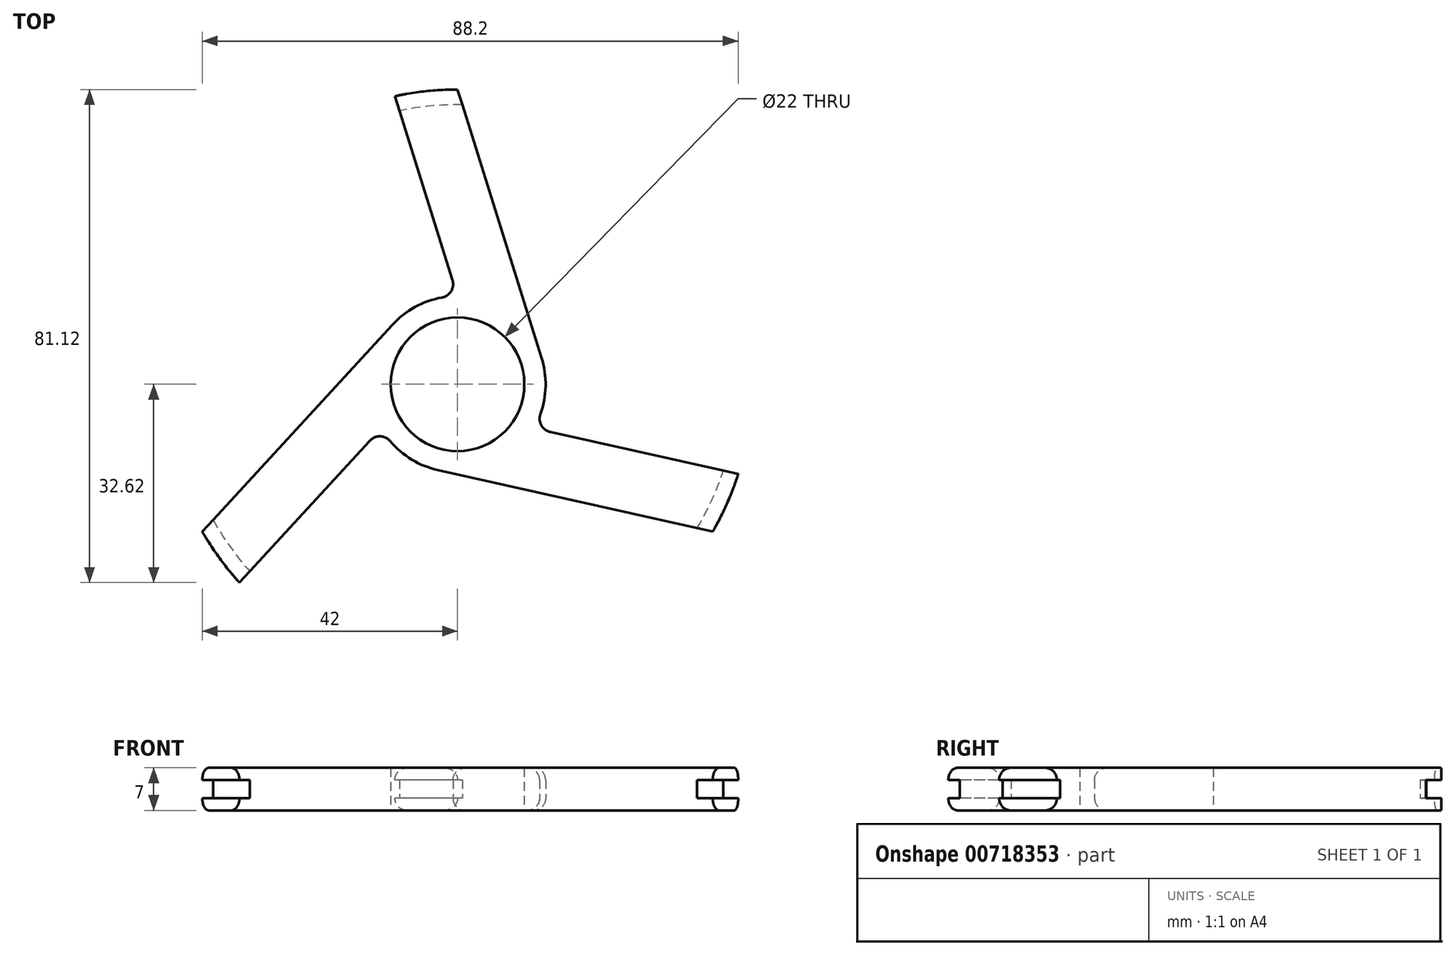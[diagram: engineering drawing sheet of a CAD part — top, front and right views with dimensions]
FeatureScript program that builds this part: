
annotation { "Feature Type Name" : "Feature", "Feature Type Description" : "" }
export const myFeature = defineFeature(function(context is Context, id is Id, definition is map)
    precondition{}
    {
        {
            var Q0;
            Q0=qCreatedBy(makeId("Top.planeOp"),FACE);
            var sketch = newSketch(context, id + "F0", { "sketchPlane" : qUnion([Q0])});
            skCircle(sketch, "E0", {"center": v(0, 0) * mm, "radius": 11 * mm});
            skArc(sketch, "E1", {"start": v(-2.57, 14.27) * mm, "mid": v(-6.99, 12.7) * mm, "end": v(-10.67, 9.82) * mm});
            skCircle(sketch, "E2", {"center": v(0, 0) * mm, "radius": 48.5 * mm});
            skLineSegment(sketch, "E3", {"start": v(13.84, 4.34) * mm, "end": v(0.79, 46) * mm});
            skLineSegment(sketch, "E4", {"start": v(-0.83, 17.14) * mm, "end": v(-9.55, 45) * mm});
            skPoint(sketch, "E5", {"position": v(13.84, 4.34) * mm});
            skArc(sketch, "E6", {"start": v(-2.57, 14.27) * mm, "mid": v(-1.05, 15.31) * mm, "end": v(-0.83, 17.14) * mm});
            skPoint(sketch, "E7", {"position": v(-0.83, 17.14) * mm});
            skPoint(sketch, "E8", {"position": v(-2.57, 14.27) * mm});
            skPoint(sketch, "E9.orphan", {"position": v(-4.02, 14.5) * mm});
            skLineSegment(sketch, "E10.1.0", {"start": v(-14.43, -9.29) * mm, "end": v(-34.2, -30.77) * mm});
            skLineSegment(sketch, "E10.1.1", {"start": v(-10.67, 9.82) * mm, "end": v(-40.22, -22.32) * mm});
            skArc(sketch, "E10.1.2", {"start": v(-11.07, -9.36) * mm, "mid": v(-12.74, -8.57) * mm, "end": v(-14.43, -9.29) * mm});
            skLineSegment(sketch, "E10.2.0", {"start": v(15.26, -7.85) * mm, "end": v(43.75, -14.22) * mm});
            skLineSegment(sketch, "E10.2.1", {"start": v(-3.16, -14.15) * mm, "end": v(39.44, -23.68) * mm});
            skArc(sketch, "E10.2.2", {"start": v(13.64, -4.91) * mm, "mid": v(13.79, -6.75) * mm, "end": v(15.26, -7.85) * mm});
            skCircle(sketch, "E11", {"center": v(0, 0) * mm, "radius": 46 * mm});
            skPoint(sketch, "E12", {"position": v(43.75, -14.22) * mm});
            skPoint(sketch, "E13", {"position": v(39.44, -23.68) * mm});
            skPoint(sketch, "E14", {"position": v(0.79, 46) * mm});
            skPoint(sketch, "E15", {"position": v(-9.55, 45) * mm});
            skPoint(sketch, "E16", {"position": v(-34.2, -30.77) * mm});
            skPoint(sketch, "E17", {"position": v(-40.22, -22.32) * mm});
            skPoint(sketch, "E18.orphan", {"position": v(-35.9, -32.62) * mm});
            skPoint(sketch, "E19.orphan", {"position": v(-42, -24.25) * mm});
            skPoint(sketch, "E20.orphan", {"position": v(46.2, -14.77) * mm});
            skPoint(sketch, "E21.orphan", {"position": v(42, -24.25) * mm});
            skPoint(sketch, "E22.orphan", {"position": v(0, 48.5) * mm});
            skPoint(sketch, "E23.orphan", {"position": v(-10.3, 47.4) * mm});
            skPoint(sketch, "E24.orphan", {"position": v(0, 14.5) * mm});
            skArc(sketch, "E25.trimOffspring", {"start": v(-11.07, -9.36) * mm, "mid": v(-7.51, -12.4) * mm, "end": v(-3.16, -14.15) * mm});
            skPoint(sketch, "E26.orphan", {"position": v(-12.56, -7.25) * mm});
            skArc(sketch, "E27.trimOffspring", {"start": v(13.64, -4.91) * mm, "mid": v(14.5, -0.3) * mm, "end": v(13.84, 4.34) * mm});
            skPoint(sketch, "E28.orphan", {"position": v(12.56, -7.25) * mm});
            skLineSegment(sketch, "E29", {"start": v(-40.22, -22.32) * mm, "end": v(-42, -24.25) * mm});
            skLineSegment(sketch, "E30", {"start": v(-34.2, -30.77) * mm, "end": v(-35.9, -32.62) * mm});
            skLineSegment(sketch, "E31", {"start": v(46.2, -14.77) * mm, "end": v(43.75, -14.22) * mm});
            skLineSegment(sketch, "E32", {"start": v(42, -24.25) * mm, "end": v(39.44, -23.68) * mm});
            skLineSegment(sketch, "E33", {"start": v(-10.3, 47.4) * mm, "end": v(-9.55, 45) * mm});
            skLineSegment(sketch, "E34", {"start": v(0, 48.5) * mm, "end": v(0.79, 46) * mm});
            skSolve(sketch);
        }
        {
            var Q0;
            Q0=makeQuery(id+"F0.imprint","IMPRINT",FACE,{"disambiguationData":[TD([[makeQuery(id+"F0.imprint","IMPRINT",EDGE,{"derivedFrom":sQuery(id+"F0.wireOp",EDGE,"E0")}),-1.0]])]});
            var Q1;
            {var subQ0=sQuery(id+"F0.wireOp",EDGE,"E33");Q1=makeQuery(id+"F0.imprint","IMPRINT",FACE,{"disambiguationData":[TD([[makeQuery(id+"F0.imprint","IMPRINT",EDGE,{"derivedFrom":subQ0}),1.0]])]});}
            var Q2;
            {var subQ0=sQuery(id+"F0.wireOp",EDGE,"E31");Q2=makeQuery(id+"F0.imprint","IMPRINT",FACE,{"disambiguationData":[TD([[makeQuery(id+"F0.imprint","IMPRINT",EDGE,{"derivedFrom":subQ0}),1.0]])]});}
            var Q3;
            {var subQ0=sQuery(id+"F0.wireOp",EDGE,"E29");Q3=makeQuery(id+"F0.imprint","IMPRINT",FACE,{"disambiguationData":[TD([[makeQuery(id+"F0.imprint","IMPRINT",EDGE,{"derivedFrom":subQ0}),1.0]])]});}
            extrude(context, id + "F1", {"entities" : qUnion([Q0, Q1, Q2, Q3]), "endBound" : BoundingType.SYMMETRIC, "depth" : 7 * mm, "offsetDistance" : 25 * mm});
        }
        {
            var Q0;
            Q0=makeQuery(id+"F1.opExtrude","CAP_EDGE",EDGE,{"disambiguationData":[OSD([sQuery(id+"F0.wireOp",EDGE,"E10.1.1")])],"isStart":false});
            var Q1;
            Q1=makeQuery(id+"F1.opExtrude","CAP_EDGE",EDGE,{"disambiguationData":[OSD([sQuery(id+"F0.wireOp",EDGE,"E1")])],"isStart":false});
            var Q2;
            Q2=makeQuery(id+"F1.opExtrude","CAP_EDGE",EDGE,{"disambiguationData":[OSD([sQuery(id+"F0.wireOp",EDGE,"E6")])],"isStart":false});
            var Q3;
            Q3=makeQuery(id+"F1.opExtrude","CAP_EDGE",EDGE,{"disambiguationData":[OSD([sQuery(id+"F0.wireOp",EDGE,"E4")])],"isStart":false});
            var Q4;
            Q4=makeQuery(id+"F1.opExtrude","CAP_EDGE",EDGE,{"disambiguationData":[OSD([sQuery(id+"F0.wireOp",EDGE,"E3")])],"isStart":false});
            var Q5;
            Q5=makeQuery(id+"F1.opExtrude","CAP_EDGE",EDGE,{"disambiguationData":[OSD([sQuery(id+"F0.wireOp",EDGE,"E27.trimOffspring")])],"isStart":false});
            var Q6;
            Q6=makeQuery(id+"F1.opExtrude","CAP_EDGE",EDGE,{"disambiguationData":[OSD([sQuery(id+"F0.wireOp",EDGE,"E10.2.2")])],"isStart":false});
            var Q7;
            Q7=makeQuery(id+"F1.opExtrude","CAP_EDGE",EDGE,{"disambiguationData":[OSD([sQuery(id+"F0.wireOp",EDGE,"E10.2.0")])],"isStart":false});
            var Q8;
            Q8=makeQuery(id+"F1.opExtrude","CAP_EDGE",EDGE,{"disambiguationData":[OSD([sQuery(id+"F0.wireOp",EDGE,"E10.2.1")])],"isStart":false});
            var Q9;
            Q9=makeQuery(id+"F1.opExtrude","CAP_EDGE",EDGE,{"disambiguationData":[OSD([sQuery(id+"F0.wireOp",EDGE,"E25.trimOffspring")])],"isStart":false});
            var Q10;
            Q10=makeQuery(id+"F1.opExtrude","CAP_EDGE",EDGE,{"disambiguationData":[OSD([sQuery(id+"F0.wireOp",EDGE,"E10.1.2")])],"isStart":false});
            var Q11;
            Q11=makeQuery(id+"F1.opExtrude","CAP_EDGE",EDGE,{"disambiguationData":[OSD([sQuery(id+"F0.wireOp",EDGE,"E10.1.0")])],"isStart":false});
            fillet(context, id + "F2", {"entities" : qUnion([Q0, Q1, Q2, Q3, Q4, Q5, Q6, Q7, Q8, Q9, Q10, Q11]), "radius" : 2 * mm, "tangentPropagation" : true, "allowEdgeOverflow" : false});
        }
        {
            var Q0;
            Q0=makeQuery(id+"F1.opExtrude","CAP_EDGE",EDGE,{"disambiguationData":[OSD([sQuery(id+"F0.wireOp",EDGE,"E10.1.1")])],"isStart":true});
            var Q1;
            Q1=makeQuery(id+"F1.opExtrude","CAP_EDGE",EDGE,{"disambiguationData":[OSD([sQuery(id+"F0.wireOp",EDGE,"E1")])],"isStart":true});
            var Q2;
            Q2=makeQuery(id+"F1.opExtrude","CAP_EDGE",EDGE,{"disambiguationData":[OSD([sQuery(id+"F0.wireOp",EDGE,"E6")])],"isStart":true});
            var Q3;
            Q3=makeQuery(id+"F1.opExtrude","CAP_EDGE",EDGE,{"disambiguationData":[OSD([sQuery(id+"F0.wireOp",EDGE,"E4")])],"isStart":true});
            var Q4;
            Q4=makeQuery(id+"F1.opExtrude","CAP_EDGE",EDGE,{"disambiguationData":[OSD([sQuery(id+"F0.wireOp",EDGE,"E3")])],"isStart":true});
            var Q5;
            Q5=makeQuery(id+"F1.opExtrude","CAP_EDGE",EDGE,{"disambiguationData":[OSD([sQuery(id+"F0.wireOp",EDGE,"E27.trimOffspring")])],"isStart":true});
            var Q6;
            Q6=makeQuery(id+"F1.opExtrude","CAP_EDGE",EDGE,{"disambiguationData":[OSD([sQuery(id+"F0.wireOp",EDGE,"E10.2.2")])],"isStart":true});
            var Q7;
            Q7=makeQuery(id+"F1.opExtrude","CAP_EDGE",EDGE,{"disambiguationData":[OSD([sQuery(id+"F0.wireOp",EDGE,"E10.2.0")])],"isStart":true});
            var Q8;
            Q8=makeQuery(id+"F1.opExtrude","CAP_EDGE",EDGE,{"disambiguationData":[OSD([sQuery(id+"F0.wireOp",EDGE,"E10.2.1")])],"isStart":true});
            var Q9;
            Q9=makeQuery(id+"F1.opExtrude","CAP_EDGE",EDGE,{"disambiguationData":[OSD([sQuery(id+"F0.wireOp",EDGE,"E25.trimOffspring")])],"isStart":true});
            var Q10;
            Q10=makeQuery(id+"F1.opExtrude","CAP_EDGE",EDGE,{"disambiguationData":[OSD([sQuery(id+"F0.wireOp",EDGE,"E10.1.2")])],"isStart":true});
            var Q11;
            Q11=makeQuery(id+"F1.opExtrude","CAP_EDGE",EDGE,{"disambiguationData":[OSD([sQuery(id+"F0.wireOp",EDGE,"E10.1.0")])],"isStart":true});
            fillet(context, id + "F3", {"entities" : qUnion([Q0, Q1, Q2, Q3, Q4, Q5, Q6, Q7, Q8, Q9, Q10, Q11]), "radius" : 2 * mm, "tangentPropagation" : true, "allowEdgeOverflow" : false});
        }
        {
            var Q0;
            Q0=makeQuery(id+"F0.imprint","IMPRINT",FACE,{"disambiguationData":[TD([[makeQuery(id+"F0.imprint","IMPRINT",EDGE,{"derivedFrom":sQuery(id+"F0.wireOp",EDGE,"E2")}),1.0]])]});
            extrude(context, id + "F4", {"entities" : qUnion([Q0]), "endBound" : BoundingType.SYMMETRIC, "depth" : 3 * mm, "offsetDistance" : 25 * mm});
        }
        {
            var Q0;
            Q0=makeQuery(id+"F4.opExtrude","SWEPT_BODY",BODY,{"disambiguationData":[OSD([sQuery(id+"F0.wireOp",EDGE,"E2"),sQuery(id+"F0.wireOp",EDGE,"E11")])]});
            var Q1;
            Q1=makeQuery(id+"F1.opExtrude","SWEPT_BODY",BODY,{"disambiguationData":[OSD([sQuery(id+"F0.wireOp",EDGE,"E0"),sQuery(id+"F0.wireOp",EDGE,"E1"),sQuery(id+"F0.wireOp",EDGE,"E2"),sQuery(id+"F0.wireOp",EDGE,"E3"),sQuery(id+"F0.wireOp",EDGE,"E4"),sQuery(id+"F0.wireOp",EDGE,"E6"),sQuery(id+"F0.wireOp",EDGE,"E10.1.0"),sQuery(id+"F0.wireOp",EDGE,"E10.1.1"),sQuery(id+"F0.wireOp",EDGE,"E10.1.2"),sQuery(id+"F0.wireOp",EDGE,"E10.2.0"),sQuery(id+"F0.wireOp",EDGE,"E10.2.1"),sQuery(id+"F0.wireOp",EDGE,"E10.2.2"),sQuery(id+"F0.wireOp",EDGE,"E25.trimOffspring"),sQuery(id+"F0.wireOp",EDGE,"E27.trimOffspring"),sQuery(id+"F0.wireOp",EDGE,"E29"),sQuery(id+"F0.wireOp",EDGE,"E30"),sQuery(id+"F0.wireOp",EDGE,"E31"),sQuery(id+"F0.wireOp",EDGE,"E32"),sQuery(id+"F0.wireOp",EDGE,"E33"),sQuery(id+"F0.wireOp",EDGE,"E34")])]});
            booleanBodies(context, id + "F5", {"operationType" : BooleanOperationType.SUBTRACTION, "tools" : qUnion([Q0]), "targets" : qUnion([Q1])});
        }
    });
